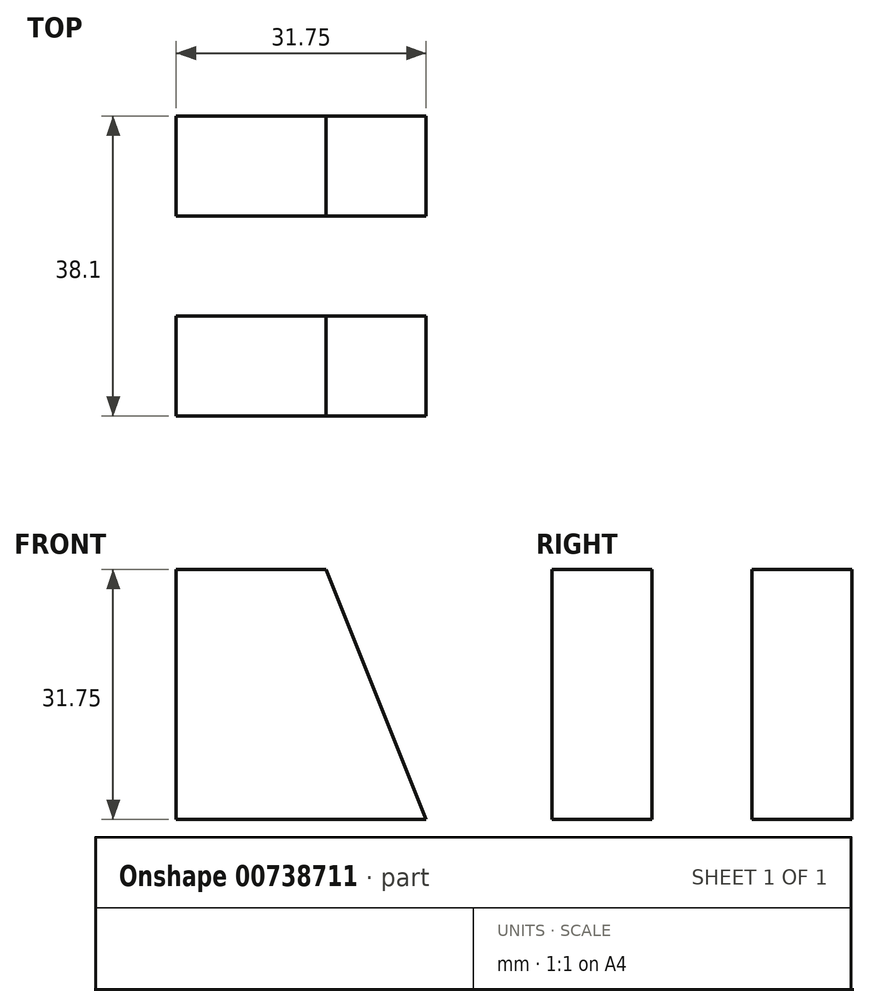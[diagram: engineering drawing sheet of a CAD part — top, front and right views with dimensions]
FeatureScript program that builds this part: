
annotation { "Feature Type Name" : "Feature", "Feature Type Description" : "" }
export const myFeature = defineFeature(function(context is Context, id is Id, definition is map)
    precondition{}
    {
        {
            var Q0;
            Q0=qCreatedBy(makeId("Front.planeOp"),FACE);
            var sketch = newSketch(context, id + "F0", { "sketchPlane" : qUnion([Q0])});
            skLineSegment(sketch, "E0", {"start": v(0, 31.75) * mm, "end": v(0, 0) * mm});
            skLineSegment(sketch, "E1", {"start": v(0, 0) * mm, "end": v(57.15, 0) * mm});
            skLineSegment(sketch, "E2", {"start": v(57.15, 0) * mm, "end": v(57.15, 31.75) * mm});
            skLineSegment(sketch, "E3", {"start": v(57.15, 31.75) * mm, "end": v(0, 31.75) * mm});
            skSolve(sketch);
        }
        {
            var Q0;
            Q0 = qSketchRegion(id + "F0", true);
            extrude(context, id + "F1", {"entities" : qUnion([Q0]), "depth" : 38.1 * mm, "offsetDistance" : 25.4 * mm});
        }
        {
            var Q0;
            Q0=qCreatedBy(makeId("Front.planeOp"),FACE);
            var sketch = newSketch(context, id + "F2", { "sketchPlane" : qUnion([Q0])});
            skLineSegment(sketch, "E4", {"start": v(19.05, 31.75) * mm, "end": v(31.75, 0) * mm});
            skLineSegment(sketch, "E5", {"start": v(31.75, 0) * mm, "end": v(57.15, 0) * mm});
            skLineSegment(sketch, "E6", {"start": v(57.15, 0) * mm, "end": v(57.15, 31.75) * mm});
            skLineSegment(sketch, "E7", {"start": v(57.15, 31.75) * mm, "end": v(19.05, 31.75) * mm});
            skSolve(sketch);
        }
        {
            var Q0;
            Q0 = qSketchRegion(id + "F2", true);
            extrude(context, id + "F3", {"entities" : qUnion([Q0]), "operationType" : NewBodyOperationType.REMOVE, "depth" : 12.7 * mm, "offsetDistance" : 25.4 * mm});
        }
        {
            var Q0;
            Q0=qCreatedBy(makeId("Front.planeOp"),FACE);
            var sketch = newSketch(context, id + "F4", { "sketchPlane" : qUnion([Q0])});
            skLineSegment(sketch, "E8", {"start": v(19.05, 31.75) * mm, "end": v(31.75, 0) * mm});
            skLineSegment(sketch, "E9", {"start": v(31.75, 0) * mm, "end": v(57.15, 0) * mm});
            skLineSegment(sketch, "E10", {"start": v(57.15, 0) * mm, "end": v(57.15, 31.75) * mm});
            skLineSegment(sketch, "E11", {"start": v(57.15, 31.75) * mm, "end": v(19.05, 31.75) * mm});
            skSolve(sketch);
        }
        {
            var Q0;
            Q0 = qSketchRegion(id + "F4", true);
            extrude(context, id + "F5", {"entities" : qUnion([Q0]), "operationType" : NewBodyOperationType.REMOVE, "endBound" : BoundingType.THROUGH_ALL, "depth" : 12.7 * mm, "offsetDistance" : 25.4 * mm});
        }
        {
            var Q0;
            Q0=qCreatedBy(makeId("Right.planeOp"),FACE);
            var sketch = newSketch(context, id + "F6", { "sketchPlane" : qUnion([Q0])});
            skLineSegment(sketch, "E12", {"start": v(-25.4, 31.75) * mm, "end": v(-25.4, 0) * mm});
            skLineSegment(sketch, "E13", {"start": v(-25.4, 0) * mm, "end": v(-12.7, 0) * mm});
            skLineSegment(sketch, "E14", {"start": v(-12.7, 0) * mm, "end": v(-12.7, 31.75) * mm});
            skLineSegment(sketch, "E15", {"start": v(-12.7, 31.75) * mm, "end": v(-25.4, 31.75) * mm});
            skSolve(sketch);
        }
        {
            var Q0;
            Q0 = qSketchRegion(id + "F6", true);
            extrude(context, id + "F7", {"entities" : qUnion([Q0]), "operationType" : NewBodyOperationType.ADD, "depth" : 57.15 * mm, "offsetDistance" : 25.4 * mm});
        }
        {
            var Q0;
            Q0=qCreatedBy(makeId("Front.planeOp"),FACE);
            var sketch = newSketch(context, id + "F8", { "sketchPlane" : qUnion([Q0])});
            skLineSegment(sketch, "E16", {"start": v(44.38, 34.29) * mm, "end": v(56.82, 0) * mm});
            skLineSegment(sketch, "E17", {"start": v(56.82, 0) * mm, "end": v(56.82, 31.75) * mm});
            skLineSegment(sketch, "E18", {"start": v(56.82, 31.75) * mm, "end": v(44.38, 34.29) * mm});
            skSolve(sketch);
        }
        {
            var Q0;
            Q0 = qSketchRegion(id + "F8", true);
            extrude(context, id + "F9", {"entities" : qUnion([Q0]), "operationType" : NewBodyOperationType.REMOVE, "endBound" : BoundingType.THROUGH_ALL, "depth" : 25.4 * mm, "offsetDistance" : 25.4 * mm});
        }
        {
            var Q0;
            Q0=qCreatedBy(makeId("Right.planeOp"),FACE);
            var sketch = newSketch(context, id + "F10", { "sketchPlane" : qUnion([Q0])});
            skSolve(sketch);
        }
        {
            var Q0;
            Q0 = qSketchRegion(id + "F10", true);
            var Q1;
            Q1=makeQuery(id+"F7.opExtrude","CAP_FACE",FACE,{"disambiguationData":[OSD([sQuery(id+"F6.wireOp",EDGE,"E12"),sQuery(id+"F6.wireOp",EDGE,"E13"),sQuery(id+"F6.wireOp",EDGE,"E14"),sQuery(id+"F6.wireOp",EDGE,"E15")])],"isStart":false});
            extrude(context, id + "F11", {"entities" : qUnion([Q0, Q1]), "operationType" : NewBodyOperationType.REMOVE, "endBound" : BoundingType.THROUGH_ALL, "oppositeDirection" : true, "depth" : 25.4 * mm, "offsetDistance" : 25.4 * mm});
        }
    });
